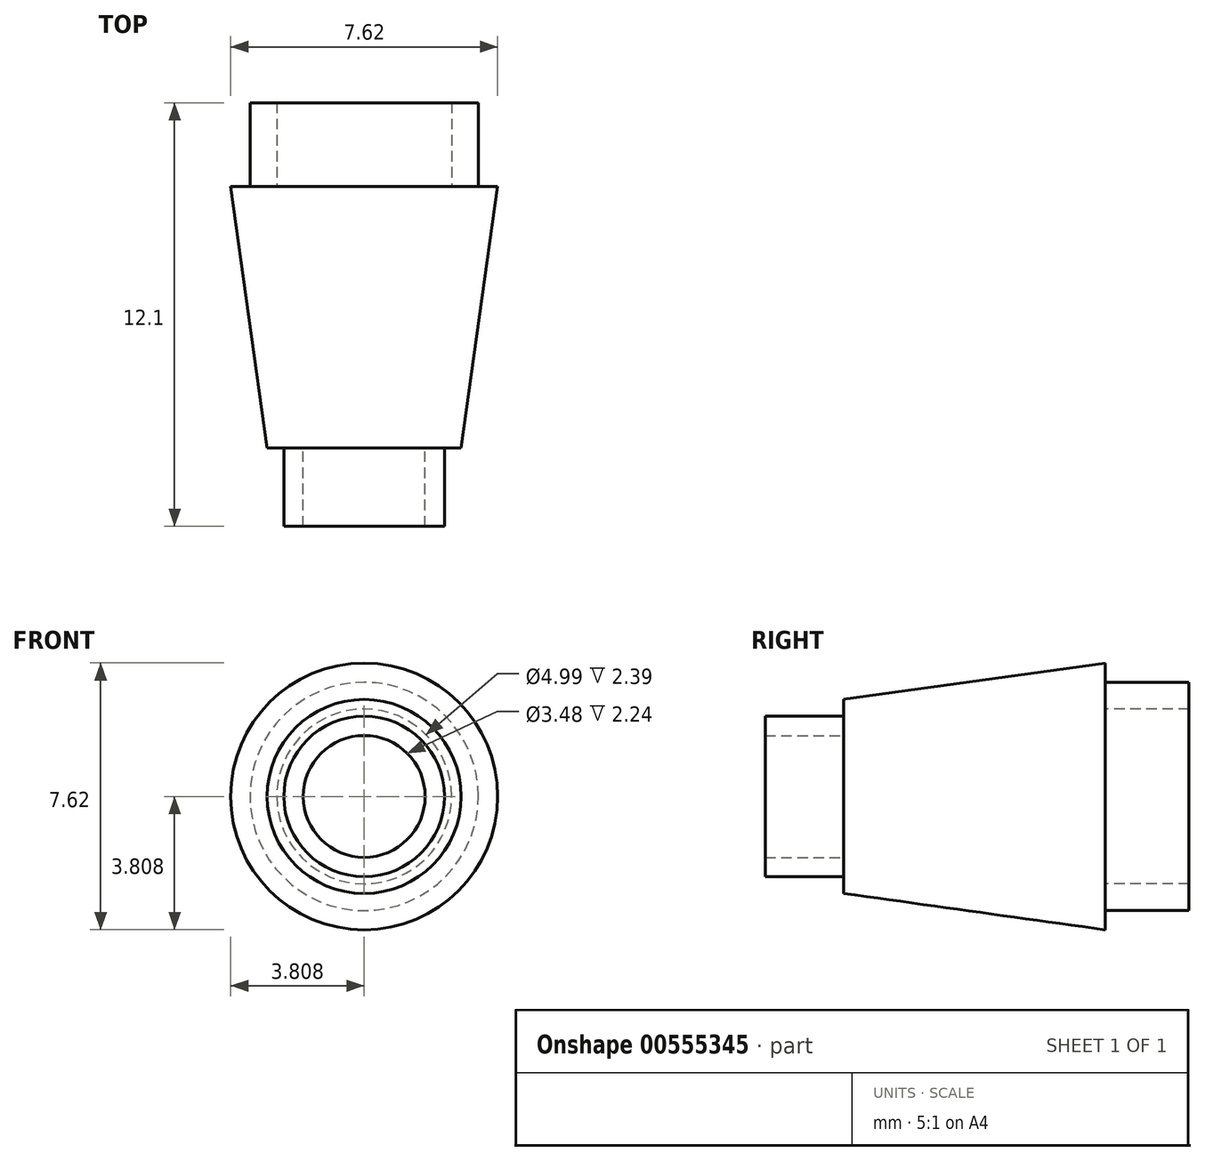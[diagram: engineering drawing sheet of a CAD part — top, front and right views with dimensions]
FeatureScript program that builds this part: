
annotation { "Feature Type Name" : "Feature", "Feature Type Description" : "" }
export const myFeature = defineFeature(function(context is Context, id is Id, definition is map)
    precondition{}
    {
        {
            var Q0;
            Q0=qCreatedBy(makeId("Front.planeOp"),FACE);
            var sketch = newSketch(context, id + "F0", { "sketchPlane" : qUnion([Q0])});
            skCircle(sketch, "E0", {"center": v(8.59, 15.99) * mm, "radius": 3.81 * mm});
            skSolve(sketch);
        }
        {
            var Q0;
            Q0 = qSketchRegion(id + "F0", true);
            extrude(context, id + "F1", {"entities" : qUnion([Q0]), "depth" : 7.47 * mm, "offsetDistance" : 25 * mm});
        }
        {
            var Q0;
            Q0=makeQuery(id+"F1.opExtrude","CAP_FACE",FACE,{"disambiguationData":[OSD([sQuery(id+"F0.wireOp",EDGE,"E0")])],"isStart":false});
            var sketch = newSketch(context, id + "F2", { "sketchPlane" : qUnion([Q0])});
            skCircle(sketch, "E1", {"center": v(8.59, 15.99) * mm, "radius": 2.77 * mm});
            skSolve(sketch);
        }
        {
            var Q1;
            Q1=makeQuery(id+"F1.opExtrude","CAP_FACE",FACE,{"disambiguationData":[OSD([sQuery(id+"F0.wireOp",EDGE,"E0")])],"isStart":true});
            var Q2;
            Q2=makeQuery(id+"F2.imprint","IMPRINT",FACE,{"disambiguationData":[TD([[makeQuery(id+"F2.imprint","IMPRINT",EDGE,{"derivedFrom":sQuery(id+"F2.wireOp",EDGE,"E1")}),1.0]])]});
            loft(context, id + "F3", {"operationType" : NewBodyOperationType.INTERSECT, "sheetProfilesArray" : [{ "sheetProfileEntities" : qUnion([Q1]) }, { "sheetProfileEntities" : qUnion([Q2]) }]});
        }
        {
            var Q0;
            Q0=makeQuery(id+"F1.opExtrude","CAP_FACE",FACE,{"disambiguationData":[OSD([sQuery(id+"F0.wireOp",EDGE,"E0")])],"isStart":true});
            var sketch = newSketch(context, id + "F4", { "sketchPlane" : qUnion([Q0])});
            skCircle(sketch, "E2", {"center": v(-8.59, 15.99) * mm, "radius": 2.5 * mm});
            skCircle(sketch, "E3", {"center": v(-8.59, 15.99) * mm, "radius": 3.26 * mm});
            skSolve(sketch);
        }
        {
            var Q0;
            Q0=makeQuery(id+"F4.imprint","IMPRINT",FACE,{"disambiguationData":[TD([[makeQuery(id+"F4.imprint","IMPRINT",EDGE,{"derivedFrom":sQuery(id+"F4.wireOp",EDGE,"E2")}),-1.0]])]});
            var Q1;
            Q1=sQuery(id+"F4.wireOp",EDGE,"E3");
            var Q2;
            Q2=sQuery(id+"F4.wireOp",EDGE,"E2");
            extrude(context, id + "F5", {"entities" : qUnion([Q0]), "surfaceEntities" : qUnion([Q1, Q2]), "depth" : 2.4 * mm, "offsetDistance" : 25 * mm});
        }
        {
            var Q0;
            Q0=makeQuery(id+"F1.opExtrude","CAP_FACE",FACE,{"disambiguationData":[OSD([sQuery(id+"F0.wireOp",EDGE,"E0")])],"isStart":false});
            var sketch = newSketch(context, id + "F6", { "sketchPlane" : qUnion([Q0])});
            skCircle(sketch, "E4", {"center": v(8.59, 15.99) * mm, "radius": 1.74 * mm});
            skCircle(sketch, "E5", {"center": v(8.59, 15.99) * mm, "radius": 2.3 * mm});
            skSolve(sketch);
        }
        {
            var Q0;
            Q0=makeQuery(id+"F6.imprint","IMPRINT",FACE,{"disambiguationData":[TD([[makeQuery(id+"F6.imprint","IMPRINT",EDGE,{"derivedFrom":sQuery(id+"F6.wireOp",EDGE,"E4")}),-1.0]])]});
            extrude(context, id + "F7", {"entities" : qUnion([Q0]), "operationType" : NewBodyOperationType.ADD, "depth" : 2.24 * mm, "offsetDistance" : 25 * mm});
        }
    });
